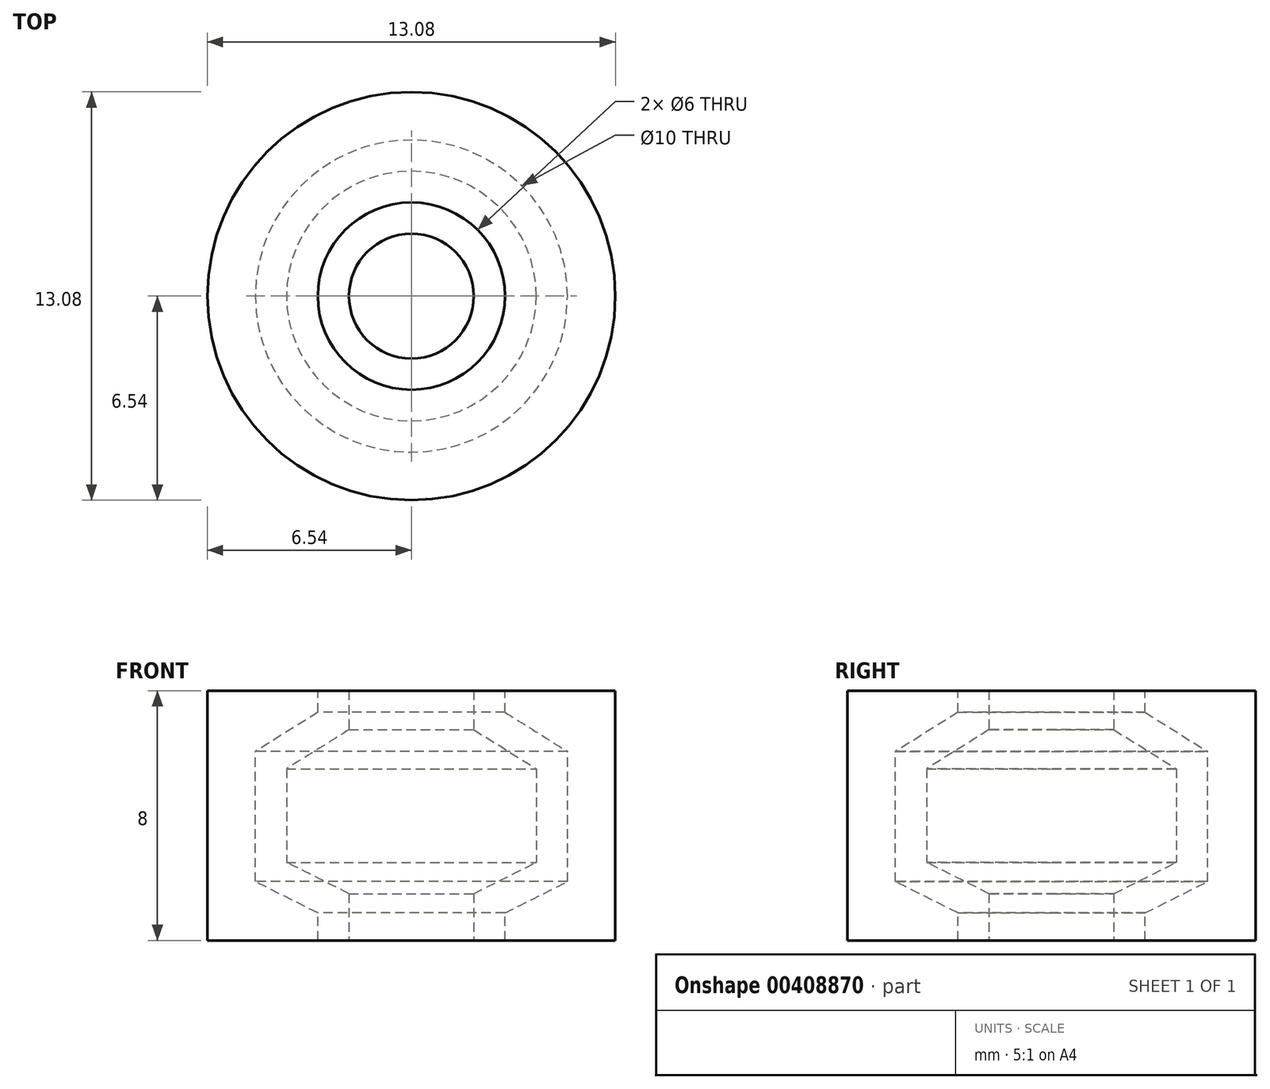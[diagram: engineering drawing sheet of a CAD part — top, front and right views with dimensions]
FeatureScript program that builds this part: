
annotation { "Feature Type Name" : "Feature", "Feature Type Description" : "" }
export const myFeature = defineFeature(function(context is Context, id is Id, definition is map)
    precondition{}
    {
        {
            var Q0;
            Q0=qCreatedBy(makeId("Front.planeOp"),FACE);
            var sketch = newSketch(context, id + "F0", { "sketchPlane" : qUnion([Q0])});
            skLineSegment(sketch, "E0", {"start": v(0, 0) * mm, "end": v(0, 8) * mm});
            skLineSegment(sketch, "E1", {"start": v(0, 8) * mm, "end": v(2, 8) * mm});
            skLineSegment(sketch, "E2", {"start": v(2, 8) * mm, "end": v(2, 0) * mm});
            skLineSegment(sketch, "E3", {"start": v(2, 0) * mm, "end": v(0, 0) * mm});
            skLineSegment(sketch, "E4", {"start": v(2, 8) * mm, "end": v(2, 5.5) * mm});
            skLineSegment(sketch, "E5", {"start": v(2, 5.5) * mm, "end": v(4, 5.5) * mm});
            skLineSegment(sketch, "E6", {"start": v(4, 5.5) * mm, "end": v(4, 4) * mm});
            skLineSegment(sketch, "E7", {"start": v(4, 4) * mm, "end": v(4, 2.5) * mm});
            skLineSegment(sketch, "E8", {"start": v(4, 2.5) * mm, "end": v(2, 2.5) * mm});
            skLineSegment(sketch, "E9", {"start": v(2, 5.5) * mm, "end": v(2, 6.75) * mm});
            skLineSegment(sketch, "E10", {"start": v(2, 6.75) * mm, "end": v(4, 5.5) * mm});
            skLineSegment(sketch, "E11", {"start": v(2, 2.5) * mm, "end": v(2, 1.5) * mm});
            skLineSegment(sketch, "E12", {"start": v(2, 1.5) * mm, "end": v(4, 2.5) * mm});
            skSolve(sketch);
        }
        {
            var Q0;
            Q0 = qSketchRegion(id + "F0", true);
            var Q1;
            Q1=sQuery(id+"F0.wireOp",EDGE,"E0");
            revolve(context, id + "F1", {"entities" : qUnion([Q0]), "axis" : qUnion([Q1]), "revolveType" : RevolveType.FULL});
        }
        {
            var Q0;
            Q0=qCreatedBy(makeId("Front.planeOp"),FACE);
            var sketch = newSketch(context, id + "F2", { "sketchPlane" : qUnion([Q0])});
            skLineSegment(sketch, "E13", {"start": v(2, 8) * mm, "end": v(2, 6.75) * mm});
            skLineSegment(sketch, "E14", {"start": v(-2, 6.75) * mm, "end": v(-2, 8) * mm});
            skLineSegment(sketch, "E15", {"start": v(2, 6.75) * mm, "end": v(4, 5.5) * mm});
            skLineSegment(sketch, "E16", {"start": v(-4, 5.5) * mm, "end": v(-2, 6.75) * mm});
            skLineSegment(sketch, "E17", {"start": v(4, 5.5) * mm, "end": v(4, 2.5) * mm});
            skLineSegment(sketch, "E18", {"start": v(-4, 2.5) * mm, "end": v(-4, 5.5) * mm});
            skLineSegment(sketch, "E19", {"start": v(2, 1.5) * mm, "end": v(2, 0) * mm});
            skLineSegment(sketch, "E20", {"start": v(-2, 0) * mm, "end": v(-2, 1.5) * mm});
            skLineSegment(sketch, "E21", {"start": v(-4, 2.5) * mm, "end": v(-2, 1.5) * mm});
            skLineSegment(sketch, "E22", {"start": v(2, 1.5) * mm, "end": v(4, 2.5) * mm});
            skLineSegment(sketch, "E23", {"start": v(-2, 8) * mm, "end": v(2, 8) * mm});
            skLineSegment(sketch, "E24", {"start": v(2, 0) * mm, "end": v(-2, 0) * mm});
            skLineSegment(sketch, "E25", {"start": v(0, 8) * mm, "end": v(0, 0) * mm});
            skLineSegment(sketch, "E26.0", {"start": v(3, 8) * mm, "end": v(3, 7.3) * mm});
            skLineSegment(sketch, "E27.0", {"start": v(3, 7.3) * mm, "end": v(4.5, 6.36) * mm});
            skLineSegment(sketch, "E28.0", {"start": v(5, 5.5) * mm, "end": v(5, 2.5) * mm});
            skLineSegment(sketch, "E29.0", {"start": v(3, 0.88) * mm, "end": v(4.44, 1.6) * mm});
            skLineSegment(sketch, "E30.0", {"start": v(3, 0.88) * mm, "end": v(3, 0) * mm});
            skLineSegment(sketch, "E31", {"start": v(2, 8) * mm, "end": v(3, 8) * mm});
            skLineSegment(sketch, "E32", {"start": v(3, 7.3) * mm, "end": v(5, 6.05) * mm});
            skLineSegment(sketch, "E33", {"start": v(5, 5.5) * mm, "end": v(5, 6.05) * mm});
            skLineSegment(sketch, "E34", {"start": v(4.44, 1.6) * mm, "end": v(5, 1.88) * mm});
            skLineSegment(sketch, "E35", {"start": v(5, 2.5) * mm, "end": v(5, 1.88) * mm});
            skLineSegment(sketch, "E36", {"start": v(2, 0) * mm, "end": v(2.54, 0) * mm});
            skLineSegment(sketch, "E37", {"start": v(2.54, 0) * mm, "end": v(6.54, 0) * mm});
            skLineSegment(sketch, "E38", {"start": v(6.54, 0) * mm, "end": v(6.54, 8) * mm});
            skLineSegment(sketch, "E39", {"start": v(6.54, 8) * mm, "end": v(3, 8) * mm});
            skLineSegment(sketch, "E40", {"start": v(5, 6.05) * mm, "end": v(5, 1.88) * mm});
            skLineSegment(sketch, "E41", {"start": v(5, 1.88) * mm, "end": v(3, 0.88) * mm});
            skSolve(sketch);
        }
        {
            var Q0;
            {var subQ3=sQuery(id+"F2.wireOp",EDGE,"E26.0");Q0=makeQuery(id+"F2.imprint","IMPRINT",FACE,{"disambiguationData":[TD([[makeQuery(id+"F2.imprint","IMPRINT",EDGE,{"derivedFrom":subQ3}),1.0]])]});}
            var Q1;
            Q1=sQuery(id+"F2.wireOp",EDGE,"E25");
            revolve(context, id + "F3", {"entities" : qUnion([Q0]), "axis" : qUnion([Q1]), "revolveType" : RevolveType.FULL});
        }
    });
